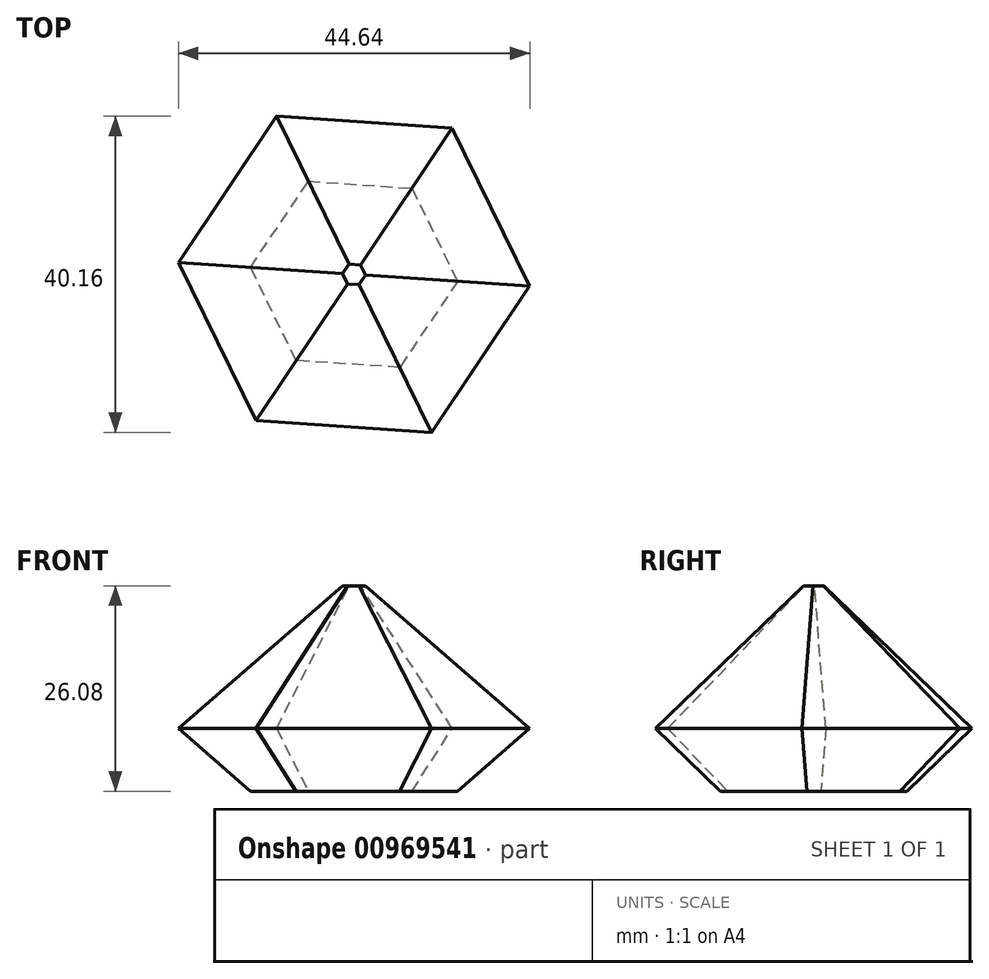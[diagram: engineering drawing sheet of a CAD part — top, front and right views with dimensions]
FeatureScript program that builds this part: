
annotation { "Feature Type Name" : "Feature", "Feature Type Description" : "" }
export const myFeature = defineFeature(function(context is Context, id is Id, definition is map)
    precondition{}
    {
        {
            var Q0;
            Q0=qCreatedBy(makeId("Top.planeOp"),FACE);
            var sketch = newSketch(context, id + "F0", { "sketchPlane" : qUnion([Q0])});
            skLineSegment(sketch, "E0.0", {"start": v(-12.26, 25) * mm, "end": v(15.52, 23.12) * mm});
            skLineSegment(sketch, "E0.1", {"start": v(15.52, 23.12) * mm, "end": v(27.78, -1.88) * mm});
            skLineSegment(sketch, "E0.2", {"start": v(27.78, -1.88) * mm, "end": v(12.26, -25) * mm});
            skLineSegment(sketch, "E0.3", {"start": v(12.26, -25) * mm, "end": v(-15.52, -23.12) * mm});
            skLineSegment(sketch, "E0.4", {"start": v(-15.52, -23.12) * mm, "end": v(-27.78, 1.88) * mm});
            skLineSegment(sketch, "E0.5", {"start": v(-27.78, 1.88) * mm, "end": v(-12.26, 25) * mm});
            skSolve(sketch);
        }
        {
            var Q0;
            Q0=makeQuery(id+"F0.imprint","IMPRINT",FACE,{"disambiguationData":[TD([[makeQuery(id+"F0.imprint","IMPRINT",EDGE,{"derivedFrom":sQuery(id+"F0.wireOp",EDGE,"E0.0")}),-1.0]])]});
            extrude(context, id + "F1", {"entities" : qUnion([Q0]), "endBound" : BoundingType.SYMMETRIC, "depth" : 76.2 * mm, "offsetDistance" : 25.4 * mm});
        }
        {
            var Q0;
            Q0=makeQuery(id+"F1.opExtrude","CAP_FACE",FACE,{"disambiguationData":[OSD([sQuery(id+"F0.wireOp",EDGE,"E0.0"),sQuery(id+"F0.wireOp",EDGE,"E0.1"),sQuery(id+"F0.wireOp",EDGE,"E0.2"),sQuery(id+"F0.wireOp",EDGE,"E0.3"),sQuery(id+"F0.wireOp",EDGE,"E0.4"),sQuery(id+"F0.wireOp",EDGE,"E0.5")])],"isStart":false});
            chamfer(context, id + "F2", {"entities" : qUnion([Q0]), "width" : 22.86 * mm, "tangentPropagation" : true});
        }
        {
            var Q0;
            Q0=qCreatedBy(makeId("Right.planeOp"),FACE);
            var sketch = newSketch(context, id + "F3", { "sketchPlane" : qUnion([Q0])});
            skLineSegment(sketch, "E1.bottom", {"start": v(46.8, 12.02) * mm, "end": v(-57.94, 12.02) * mm});
            skLineSegment(sketch, "E1.top", {"start": v(46.8, -61.3) * mm, "end": v(-57.94, -61.3) * mm});
            skLineSegment(sketch, "E1.left", {"start": v(46.8, 12.02) * mm, "end": v(46.8, -61.3) * mm});
            skLineSegment(sketch, "E1.right", {"start": v(-57.94, 12.02) * mm, "end": v(-57.94, -61.3) * mm});
            skSolve(sketch);
        }
        {
            var Q0;
            Q0 = qSketchRegion(id + "F3", true);
            extrude(context, id + "F4", {"entities" : qUnion([Q0]), "operationType" : NewBodyOperationType.REMOVE, "endBound" : BoundingType.SYMMETRIC, "depth" : 76.2 * mm, "offsetDistance" : 25.4 * mm});
        }
        {
            var Q0;
            Q0=makeQuery(id+"F4.boolean.opBoolean","COPY",FACE,{"derivedFrom":makeQuery(id+"F4.opExtrude","SWEPT_FACE",FACE,{"disambiguationData":[OSD([sQuery(id+"F3.wireOp",EDGE,"E1.bottom")])]})});
            chamfer(context, id + "F5", {"entities" : qUnion([Q0]), "width" : 12.7 * mm, "tangentPropagation" : true});
        }
    });
